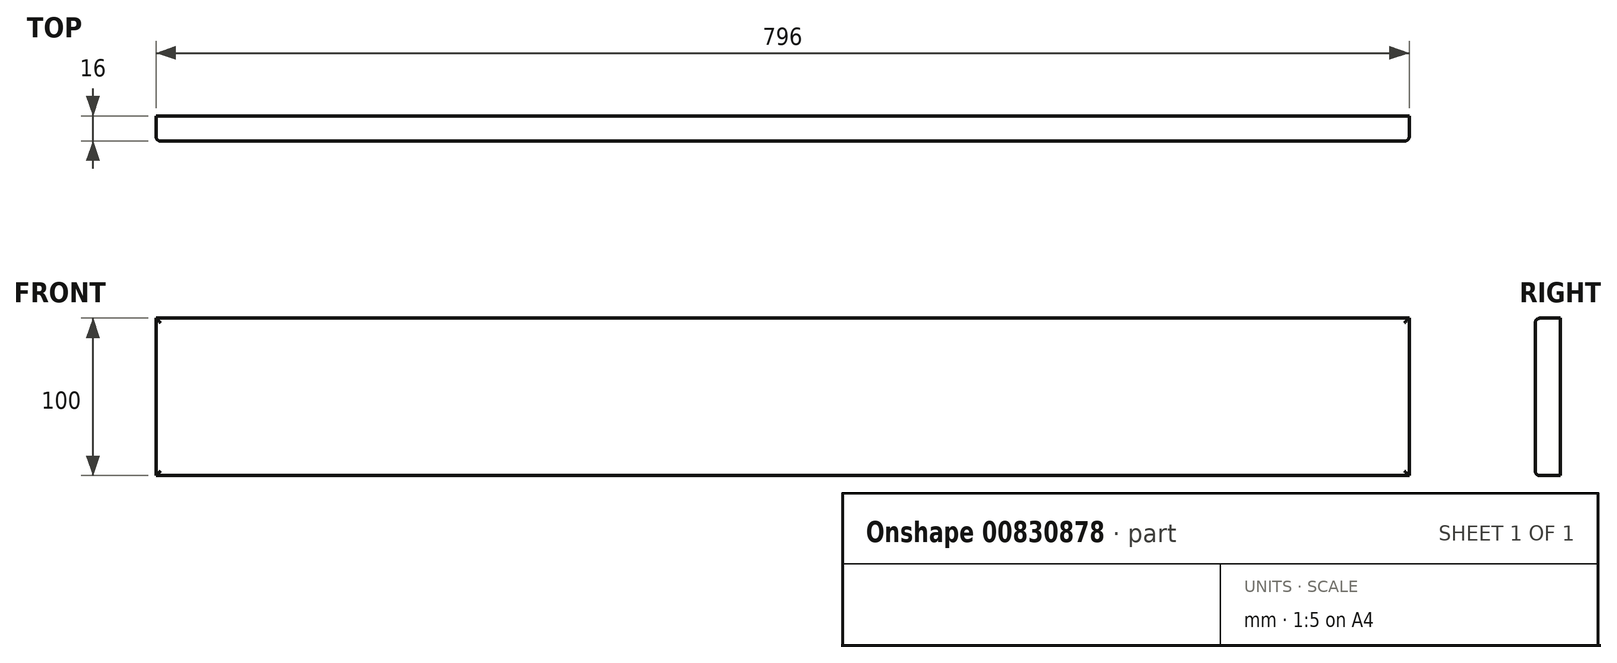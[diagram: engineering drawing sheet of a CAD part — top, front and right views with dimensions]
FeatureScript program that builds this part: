
annotation { "Feature Type Name" : "Feature", "Feature Type Description" : "" }
export const myFeature = defineFeature(function(context is Context, id is Id, definition is map)
    precondition{}
    {
        {
            var Q0;
            Q0=qCreatedBy(makeId("Front.planeOp"),FACE);
            var sketch = newSketch(context, id + "F0", { "sketchPlane" : qUnion([Q0])});
            skLineSegment(sketch, "E0.bottom", {"start": v(0, 0) * mm, "end": v(53.67, 0) * mm});
            skLineSegment(sketch, "E0.top", {"start": v(0, 36.38) * mm, "end": v(53.67, 36.38) * mm});
            skLineSegment(sketch, "E0.left", {"start": v(0, 0) * mm, "end": v(0, 36.38) * mm});
            skLineSegment(sketch, "E0.right", {"start": v(53.67, 0) * mm, "end": v(53.67, 36.38) * mm});
            skSolve(sketch);
        }
        {
            var Q0;
            Q0=makeQuery(id+"F0.imprint","IMPRINT",FACE,{"disambiguationData":[TD([[makeQuery(id+"F0.imprint","IMPRINT",EDGE,{"derivedFrom":sQuery(id+"F0.wireOp",EDGE,"E0.bottom")}),1.0]])]});
            extrude(context, id + "F1", {"entities" : qUnion([Q0]), "depth" : 16 * mm, "offsetDistance" : 25.4 * mm});
        }
        {
            var Q0;
            Q0=makeQuery(id+"F1.opExtrude","SWEPT_FACE",FACE,{"disambiguationData":[OSD([sQuery(id+"F0.wireOp",EDGE,"E0.left")])]});
            extrude(context, id + "F2", {"entities" : qUnion([Q0]), "operationType" : NewBodyOperationType.ADD, "oppositeDirection" : true, "depth" : 396 * mm, "offsetDistance" : 25 * mm});
        }
        {
            var Q0;
            {var subQ0=sQuery(id+"F0.wireOp",EDGE,"E0.bottom");Q0=makeQuery(id+"F2.boolean.opBoolean","MERGE",FACE,{"derivedFrom":[makeQuery(id+"F1.opExtrude","SWEPT_FACE",FACE,{"disambiguationData":[OSD([subQ0])]}),makeQuery(id+"F2.opExtrude","SWEPT_FACE",FACE,{"disambiguationData":[OSD([subQ0,sQuery(id+"F0.wireOp",EDGE,"E0.left")])]})]});}
            extrude(context, id + "F3", {"entities" : qUnion([Q0]), "operationType" : NewBodyOperationType.ADD, "oppositeDirection" : true, "depth" : 100 * mm, "offsetDistance" : 25 * mm});
        }
        {
            var Q0;
            {var subQ0=sQuery(id+"F0.wireOp",EDGE,"E0.left");var subQ1=sQuery(id+"F0.wireOp",EDGE,"E0.bottom");Q0=makeQuery(id+"F3.boolean.opBoolean","MERGE",FACE,{"derivedFrom":[makeQuery(id+"F2.opExtrude","CAP_FACE",FACE,{"disambiguationData":[OSD([subQ0])],"isStart":false}),makeQuery(id+"F3.opExtrude","SWEPT_FACE",FACE,{"disambiguationData":[OSD([subQ1,subQ0]),TDD([makeQuery(id+"F2.opExtrude","CAP_EDGE",EDGE,{"disambiguationData":[OSD([subQ1,subQ0])],"isStart":false})])]})]});}
            extrude(context, id + "F4", {"entities" : qUnion([Q0]), "operationType" : NewBodyOperationType.ADD, "depth" : 200 * mm, "offsetDistance" : 25 * mm});
        }
        {
            var Q0;
            Q0=makeQuery(id+"F4.opExtrude","CAP_FACE",FACE,{"disambiguationData":[OSD([sQuery(id+"F0.wireOp",EDGE,"E0.bottom"),sQuery(id+"F0.wireOp",EDGE,"E0.left")])],"isStart":false});
            extrude(context, id + "F5", {"entities" : qUnion([Q0]), "operationType" : NewBodyOperationType.ADD, "depth" : 200 * mm, "offsetDistance" : 25 * mm});
        }
        {
            var Q0;
            {var subQ0=sQuery(id+"F0.wireOp",EDGE,"E0.left");var subQ1=sQuery(id+"F0.wireOp",EDGE,"E0.bottom");var subQ2=makeQuery(id+"F1.opExtrude","CAP_VERTEX",VERTEX,{"disambiguationData":[OSD([subQ1,subQ0])],"isStart":false});var subQ3=makeQuery(id+"F1.opExtrude","CAP_EDGE",EDGE,{"disambiguationData":[OSD([subQ0])],"isStart":false});var subQ4=makeQuery(id+"F3.boolean.opBoolean","MERGE",EDGE,{"derivedFrom":[makeQuery(id+"F2.opExtrude","CAP_EDGE",EDGE,{"disambiguationData":[OSD([subQ0]),TDD([subQ3])],"isStart":false}),makeQuery(id+"F3.opExtrude","SWEPT_EDGE",EDGE,{"disambiguationData":[OSD([subQ1,subQ0]),TDD([makeQuery(id+"F2.opExtrude","CAP_VERTEX",VERTEX,{"disambiguationData":[OSD([subQ1,subQ0]),TDD([subQ2])],"isStart":false})])]})]});Q0=makeQuery(id+"F5.boolean.opBoolean","MERGE",FACE,{"derivedFrom":[makeQuery(id+"F4.boolean.opBoolean","MERGE",FACE,{"derivedFrom":[makeQuery(id+"F3.boolean.opBoolean","MERGE",FACE,{"derivedFrom":[makeQuery(id+"F2.boolean.opBoolean","MERGE",FACE,{"derivedFrom":[makeQuery(id+"F1.opExtrude","CAP_FACE",FACE,{"disambiguationData":[OSD([subQ1,sQuery(id+"F0.wireOp",EDGE,"E0.top"),subQ0,sQuery(id+"F0.wireOp",EDGE,"E0.right")])],"isStart":false}),makeQuery(id+"F2.opExtrude","SWEPT_FACE",FACE,{"disambiguationData":[OSD([subQ0]),TDD([subQ3])]})]}),makeQuery(id+"F3.opExtrude","SWEPT_FACE",FACE,{"disambiguationData":[OSD([subQ1,subQ0]),TDD([makeQuery(id+"F2.boolean.opBoolean","MERGE",EDGE,{"derivedFrom":[makeQuery(id+"F1.opExtrude","CAP_EDGE",EDGE,{"disambiguationData":[OSD([subQ1])],"isStart":false}),makeQuery(id+"F2.opExtrude","SWEPT_EDGE",EDGE,{"disambiguationData":[OSD([subQ1,subQ0]),TDD([subQ2])]})]})])]})]}),makeQuery(id+"F4.opExtrude","SWEPT_FACE",FACE,{"disambiguationData":[OSD([subQ1,subQ0]),TDD([subQ4])]})]}),makeQuery(id+"F5.opExtrude","SWEPT_FACE",FACE,{"disambiguationData":[OSD([subQ1,subQ0]),TDD([makeQuery(id+"F4.opExtrude","CAP_EDGE",EDGE,{"disambiguationData":[OSD([subQ1,subQ0]),TDD([subQ4])],"isStart":false})])]})]});}
            fillet(context, id + "F6", {"entities" : qUnion([Q0]), "radius" : 3 * mm, "tangentPropagation" : true, "allowEdgeOverflow" : false});
        }
    });
